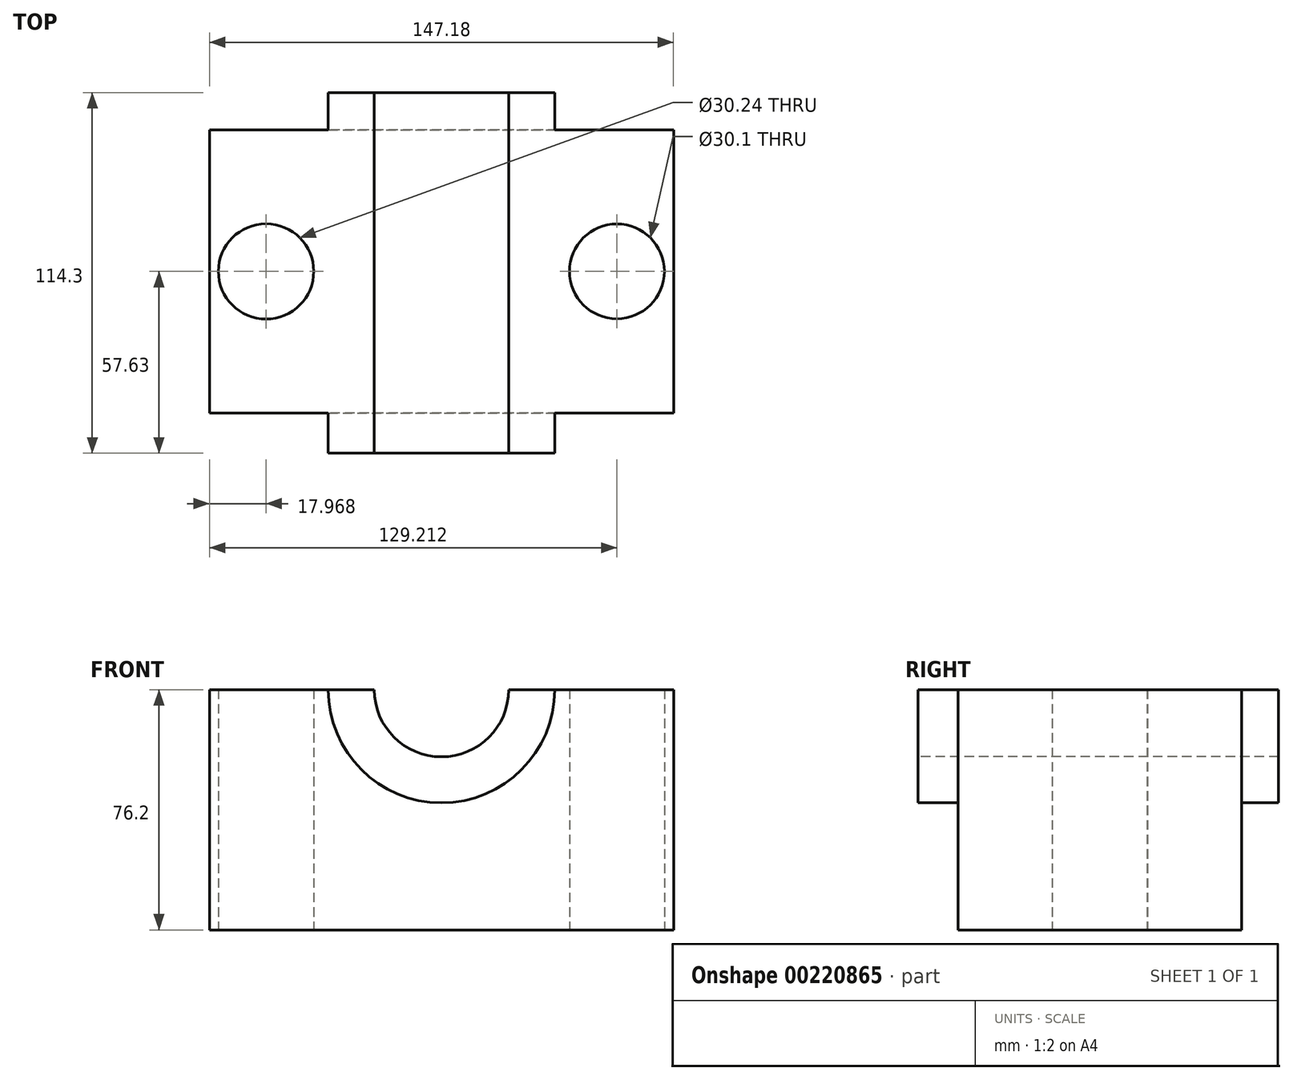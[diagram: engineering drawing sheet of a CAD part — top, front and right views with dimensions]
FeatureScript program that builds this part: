
annotation { "Feature Type Name" : "Feature", "Feature Type Description" : "" }
export const myFeature = defineFeature(function(context is Context, id is Id, definition is map)
    precondition{}
    {
        {
            var Q0;
            Q0=qCreatedBy(makeId("Top.planeOp"),FACE);
            var sketch = newSketch(context, id + "F0", { "sketchPlane" : qUnion([Q0])});
            skLineSegment(sketch, "E0.bottom", {"start": v(73.6, 44.93) * mm, "end": v(-73.6, 44.93) * mm});
            skLineSegment(sketch, "E0.top", {"start": v(73.6, -44.93) * mm, "end": v(-73.6, -44.93) * mm});
            skLineSegment(sketch, "E0.left", {"start": v(73.6, 44.93) * mm, "end": v(73.6, -44.93) * mm});
            skLineSegment(sketch, "E0.right", {"start": v(-73.6, 44.93) * mm, "end": v(-73.6, -44.93) * mm});
            skPoint(sketch, "E0.middle", {"position": v(0, 0) * mm});
            skCircle(sketch, "E1", {"center": v(-55.62, 0) * mm, "radius": 15.12 * mm});
            skCircle(sketch, "E2", {"center": v(55.62, 0) * mm, "radius": 15.05 * mm});
            skSolve(sketch);
        }
        {
            var Q0;
            Q0=makeQuery(id+"F0.imprint","IMPRINT",FACE,{"disambiguationData":[TD([[makeQuery(id+"F0.imprint","IMPRINT",EDGE,{"derivedFrom":sQuery(id+"F0.wireOp",EDGE,"E0.bottom")}),1.0]])]});
            extrude(context, id + "F1", {"entities" : qUnion([Q0]), "depth" : 76.2 * mm});
        }
        {
            var Q0;
            Q0=makeQuery(id+"F1.opExtrude","SWEPT_FACE",FACE,{"disambiguationData":[OSD([sQuery(id+"F0.wireOp",EDGE,"E0.top")])]});
            var sketch = newSketch(context, id + "F2", { "sketchPlane" : qUnion([Q0])});
            skCircle(sketch, "E3", {"center": v(0, 76.2) * mm, "radius": 35.9 * mm});
            skSolve(sketch);
        }
        {
            var Q0;
            {var subQ0=sQuery(id+"F2.wireOp",EDGE,"E3");var subQ1=makeQuery(id+"F1.opExtrude","CAP_EDGE",EDGE,{"disambiguationData":[OSD([sQuery(id+"F0.wireOp",EDGE,"E0.top")])],"isStart":false});var subQ2=makeQuery(id+"F2.imprint","INTERSECT",VERTEX,{"disambiguationData":[OD(0.0)],"derivedFrom":[subQ1,subQ0]});Q0=makeQuery(id+"F2.imprint","IMPRINT",FACE,{"disambiguationData":[TD([[makeQuery(id+"F2.imprint","IMPRINT",EDGE,{"disambiguationData":[TD([[subQ2,1.0]])],"derivedFrom":subQ0}),1.0]])]});}
            extrude(context, id + "F3", {"entities" : qUnion([Q0]), "operationType" : NewBodyOperationType.ADD, "oppositeDirection" : true, "depth" : 101.6 * mm});
        }
        {
            var Q0;
            {var subQ0=sQuery(id+"F2.wireOp",EDGE,"E3");var subQ1=makeQuery(id+"F1.opExtrude","CAP_EDGE",EDGE,{"disambiguationData":[OSD([sQuery(id+"F0.wireOp",EDGE,"E0.top")])],"isStart":false});var subQ2=makeQuery(id+"F2.imprint","INTERSECT",VERTEX,{"disambiguationData":[OD(0.0)],"derivedFrom":[subQ1,subQ0]});Q0=makeQuery(id+"F2.imprint","IMPRINT",FACE,{"disambiguationData":[TD([[makeQuery(id+"F2.imprint","IMPRINT",EDGE,{"disambiguationData":[TD([[subQ2,1.0]])],"derivedFrom":subQ0}),1.0]])]});}
            extrude(context, id + "F4", {"entities" : qUnion([Q0]), "operationType" : NewBodyOperationType.ADD, "depth" : 12.7 * mm});
        }
        {
            var Q0;
            Q0=makeQuery(id+"F4.opExtrude","CAP_FACE",FACE,{"disambiguationData":[OSD([sQuery(id+"F0.wireOp",EDGE,"E0.top"),sQuery(id+"F2.wireOp",EDGE,"E3")])],"isStart":false});
            var sketch = newSketch(context, id + "F5", { "sketchPlane" : qUnion([Q0])});
            skCircle(sketch, "E4", {"center": v(0, 76.2) * mm, "radius": 21.3 * mm});
            skSolve(sketch);
        }
        {
            var Q0;
            {var subQ0=sQuery(id+"F5.wireOp",EDGE,"E4");var subQ1=makeQuery(id+"F4.opExtrude","CAP_EDGE",EDGE,{"disambiguationData":[OSD([sQuery(id+"F0.wireOp",EDGE,"E0.top")])],"isStart":false});var subQ2=makeQuery(id+"F5.imprint","INTERSECT",VERTEX,{"disambiguationData":[OD(0.0)],"derivedFrom":[subQ1,subQ0]});Q0=makeQuery(id+"F5.imprint","IMPRINT",FACE,{"disambiguationData":[TD([[makeQuery(id+"F5.imprint","IMPRINT",EDGE,{"disambiguationData":[TD([[subQ2,-1.0]])],"derivedFrom":subQ0}),1.0]])]});}
            var Q1;
            {var subQ0=sQuery(id+"F5.wireOp",EDGE,"E4");var subQ1=makeQuery(id+"F4.opExtrude","CAP_EDGE",EDGE,{"disambiguationData":[OSD([sQuery(id+"F0.wireOp",EDGE,"E0.top")])],"isStart":false});var subQ2=makeQuery(id+"F5.imprint","INTERSECT",VERTEX,{"disambiguationData":[OD(0.0)],"derivedFrom":[subQ1,subQ0]});Q1=makeQuery(id+"F5.imprint","IMPRINT",FACE,{"disambiguationData":[TD([[makeQuery(id+"F5.imprint","IMPRINT",EDGE,{"disambiguationData":[TD([[subQ2,1.0]])],"derivedFrom":subQ0}),1.0]])]});}
            extrude(context, id + "F6", {"entities" : qUnion([Q0, Q1]), "operationType" : NewBodyOperationType.REMOVE, "endBound" : BoundingType.THROUGH_ALL, "oppositeDirection" : true, "depth" : 25.4 * mm});
        }
    });
